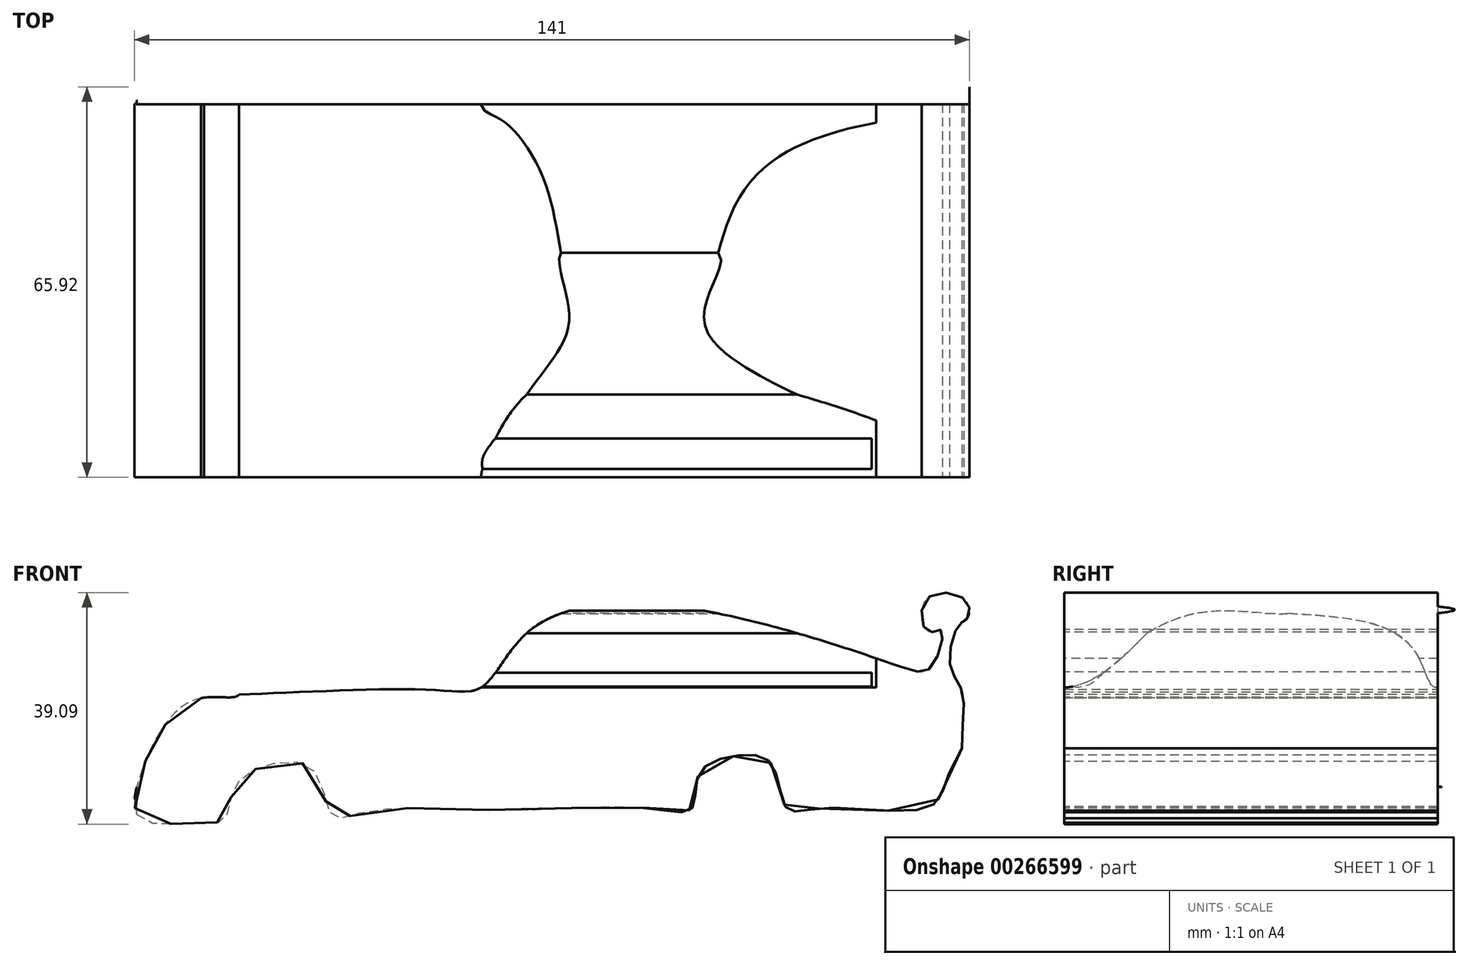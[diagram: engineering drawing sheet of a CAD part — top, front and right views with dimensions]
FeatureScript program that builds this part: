
annotation { "Feature Type Name" : "Feature", "Feature Type Description" : "" }
export const myFeature = defineFeature(function(context is Context, id is Id, definition is map)
    precondition{}
    {
        {
            var Q0;
            Q0=qCreatedBy(makeId("Top.planeOp"),FACE);
            var sketch = newSketch(context, id + "F0", { "sketchPlane" : qUnion([Q0])});
            skLineSegment(sketch, "E0.bottom", {"start": v(-32.6, 70.43) * mm, "end": v(119.8, 70.43) * mm});
            skLineSegment(sketch, "E0.top", {"start": v(-32.6, -18.47) * mm, "end": v(119.8, -18.47) * mm});
            skLineSegment(sketch, "E0.left", {"start": v(-32.6, 70.43) * mm, "end": v(-32.6, -18.47) * mm});
            skLineSegment(sketch, "E0.right", {"start": v(119.8, 70.43) * mm, "end": v(119.8, -18.47) * mm});
            skSolve(sketch);
        }
        {
            var Q0;
            Q0 = qSketchRegion(id + "F0", true);
            extrude(context, id + "F1", {"entities" : qUnion([Q0]), "depth" : 101.6 * mm});
        }
        {
            var Q0;
            Q0=makeQuery(id+"F1.opExtrude","SWEPT_FACE",FACE,{"disambiguationData":[OSD([sQuery(id+"F0.wireOp",EDGE,"E0.top")])]});
            var sketch = newSketch(context, id + "F2", { "sketchPlane" : qUnion([Q0])});
            skPoint(sketch, "E1.7.internal.snap0", {"position": v(-32.6, 50.8) * mm});
            skPoint(sketch, "E1.8.internal.snap0", {"position": v(-32.6, 50.8) * mm});
            skPoint(sketch, "E1.15.internal.snap0", {"position": v(-32.6, 50.8) * mm});
            skFitSpline(sketch, "E1", {"points": [v(-32.6, 40.34) * mm, v(-24.88, 43.4) * mm, v(-8.9, 46.17) * mm, v(20.57, 46.78) * mm, v(28.55, 47.4) * mm, v(36.23, 56.6) * mm, v(61.1, 60.9) * mm, v(98.87, 50.8) * mm, v(104.4, 50.8) * mm, v(105.93, 56.92) * mm, v(103.78, 56.6) * mm, v(103.47, 62.14) * mm, v(110.23, 61.83) * mm, v(110.23, 58.76) * mm, v(109, 57.84) * mm, v(107.47, 50.8) * mm, v(109.61, 46.17) * mm, v(110.23, 33.27) * mm, v(119.8, 32.66) * mm, v(119.8, 101.6) * mm, v(-32.6, 101.6) * mm, v(-32.6, 40.34) * mm]});
            skSolve(sketch);
        }
        {
            var Q0;
            Q0 = qSketchRegion(id + "F2", true);
            extrude(context, id + "F3", {"entities" : qUnion([Q0]), "operationType" : NewBodyOperationType.REMOVE, "oppositeDirection" : true, "depth" : 152.4 * mm});
        }
        {
            var Q0;
            Q0=makeQuery(id+"F1.opExtrude","SWEPT_FACE",FACE,{"disambiguationData":[OSD([sQuery(id+"F0.wireOp",EDGE,"E0.top")])]});
            var sketch = newSketch(context, id + "F4", { "sketchPlane" : qUnion([Q0])});
            skFitSpline(sketch, "E2", {"points": [v(-12.6, 46.01) * mm, v(-19.04, 45.41) * mm, v(-25.49, 40.34) * mm, v(-28.87, 33.58) * mm, v(-29.48, 25.29) * mm, v(-19.66, 24.37) * mm, v(-15.05, 24.98) * mm, v(-13.51, 29.9) * mm, v(-8.6, 33.89) * mm, v(0, 33.27) * mm, v(3.07, 25.6) * mm, v(8.6, 26.21) * mm, v(32.24, 26.52) * mm, v(56.5, 26.82) * mm, v(63.86, 26.82) * mm, v(65.1, 32.66) * mm, v(71.85, 35.73) * mm, v(77.37, 34.2) * mm, v(79.83, 26.82) * mm, v(85.66, 26.82) * mm, v(104.09, 27.13) * mm, v(109.46, 36.91) * mm, v(153.22, 60.6) * mm, v(140.93, 5.94) * mm, v(36.23, -16.78) * mm, v(-55.89, 2.87) * mm, v(-35.32, 45.25) * mm, v(-19.04, 52) * mm, v(-12.6, 46.01) * mm]});
            skSolve(sketch);
        }
        {
            var Q0;
            Q0 = qSketchRegion(id + "F4", true);
            extrude(context, id + "F5", {"entities" : qUnion([Q0]), "operationType" : NewBodyOperationType.REMOVE, "oppositeDirection" : true, "depth" : 152.4 * mm});
        }
        {
            var Q0;
            Q0=qCreatedBy(makeId("Top.planeOp"),FACE);
            var sketch = newSketch(context, id + "F6", { "sketchPlane" : qUnion([Q0])});
            skLineSegment(sketch, "E3", {"start": v(-29.85, 44.55) * mm, "end": v(110.69, 44.55) * mm});
            skLineSegment(sketch, "E4", {"start": v(-29.85, 44.55) * mm, "end": v(-29.85, 72.71) * mm});
            skLineSegment(sketch, "E5", {"start": v(-29.85, 72.71) * mm, "end": v(111.25, 72.71) * mm});
            skLineSegment(sketch, "E6", {"start": v(111.25, 72.71) * mm, "end": v(110.69, 44.55) * mm});
            skSolve(sketch);
        }
        {
            var Q0;
            Q0 = qSketchRegion(id + "F6", true);
            extrude(context, id + "F7", {"entities" : qUnion([Q0]), "operationType" : NewBodyOperationType.REMOVE, "depth" : 101.6 * mm});
        }
        {
            var Q0;
            Q0=qCreatedBy(makeId("Right.planeOp"),FACE);
            var sketch = newSketch(context, id + "F8", { "sketchPlane" : qUnion([Q0])});
            skLineSegment(sketch, "E7", {"start": v(45.17, 30.6) * mm, "end": v(45.17, 25.87) * mm});
            skLineSegment(sketch, "E8", {"start": v(45.17, 25.87) * mm, "end": v(72.22, 25.87) * mm});
            skLineSegment(sketch, "E9", {"start": v(72.22, 25.87) * mm, "end": v(71.38, 32.28) * mm});
            skLineSegment(sketch, "E10", {"start": v(71.38, 32.28) * mm, "end": v(45.17, 30.6) * mm});
            skSolve(sketch);
        }
        {
            var Q0;
            Q0 = qSketchRegion(id + "F8", true);
            extrude(context, id + "F9", {"entities" : qUnion([Q0]), "operationType" : NewBodyOperationType.REMOVE, "oppositeDirection" : true, "depth" : 50.8 * mm});
        }
        {
            var Q0;
            Q0=qCreatedBy(makeId("Right.planeOp"),FACE);
            var sketch = newSketch(context, id + "F10", { "sketchPlane" : qUnion([Q0])});
            skLineSegment(sketch, "E11", {"start": v(44.58, 30.38) * mm, "end": v(44.58, 25.08) * mm});
            skLineSegment(sketch, "E12", {"start": v(44.58, 25.08) * mm, "end": v(68.28, 20.62) * mm});
            skLineSegment(sketch, "E13", {"start": v(68.28, 20.62) * mm, "end": v(74.42, 28.42) * mm});
            skLineSegment(sketch, "E14", {"start": v(74.42, 28.42) * mm, "end": v(44.58, 30.38) * mm});
            skSolve(sketch);
        }
        {
            var Q0;
            Q0 = qSketchRegion(id + "F10", true);
            extrude(context, id + "F11", {"entities" : qUnion([Q0]), "operationType" : NewBodyOperationType.REMOVE, "oppositeDirection" : true, "depth" : 50.8 * mm});
        }
        {
            var Q0;
            Q0=qCreatedBy(makeId("Right.planeOp"),FACE);
            var sketch = newSketch(context, id + "F12", { "sketchPlane" : qUnion([Q0])});
            skFitSpline(sketch, "E15", {"points": [v(44.57, 47.21) * mm, v(41.52, 51.9) * mm, v(33.08, 58.12) * mm, v(10.45, 60.46) * mm, v(0, 60.23) * mm, v(-18.4, 47.21) * mm, v(-35.04, 61.16) * mm, v(-18.4, 71.13) * mm, v(49.96, 70.9) * mm, v(44.57, 47.21) * mm]});
            skSolve(sketch);
        }
        {
            var Q0;
            Q0 = qSketchRegion(id + "F12", true);
            extrude(context, id + "F13", {"entities" : qUnion([Q0]), "operationType" : NewBodyOperationType.REMOVE, "depth" : 95 * mm});
        }
        {
            var Q0;
            Q0=qCreatedBy(makeId("Right.planeOp"),FACE);
            var sketch = newSketch(context, id + "F14", { "sketchPlane" : qUnion([Q0])});
            skFitSpline(sketch, "E16", {"points": [v(20, 60) * mm, v(5.53, 60) * mm, v(-10.26, 51.59) * mm, v(-17.1, 47.37) * mm, v(-33.43, 62.64) * mm, v(2.37, 69.48) * mm, v(20, 60) * mm]});
            skSolve(sketch);
        }
        {
            var Q0;
            Q0 = qSketchRegion(id + "F14", true);
            extrude(context, id + "F15", {"entities" : qUnion([Q0]), "operationType" : NewBodyOperationType.REMOVE, "depth" : 94.23 * mm});
        }
    });
